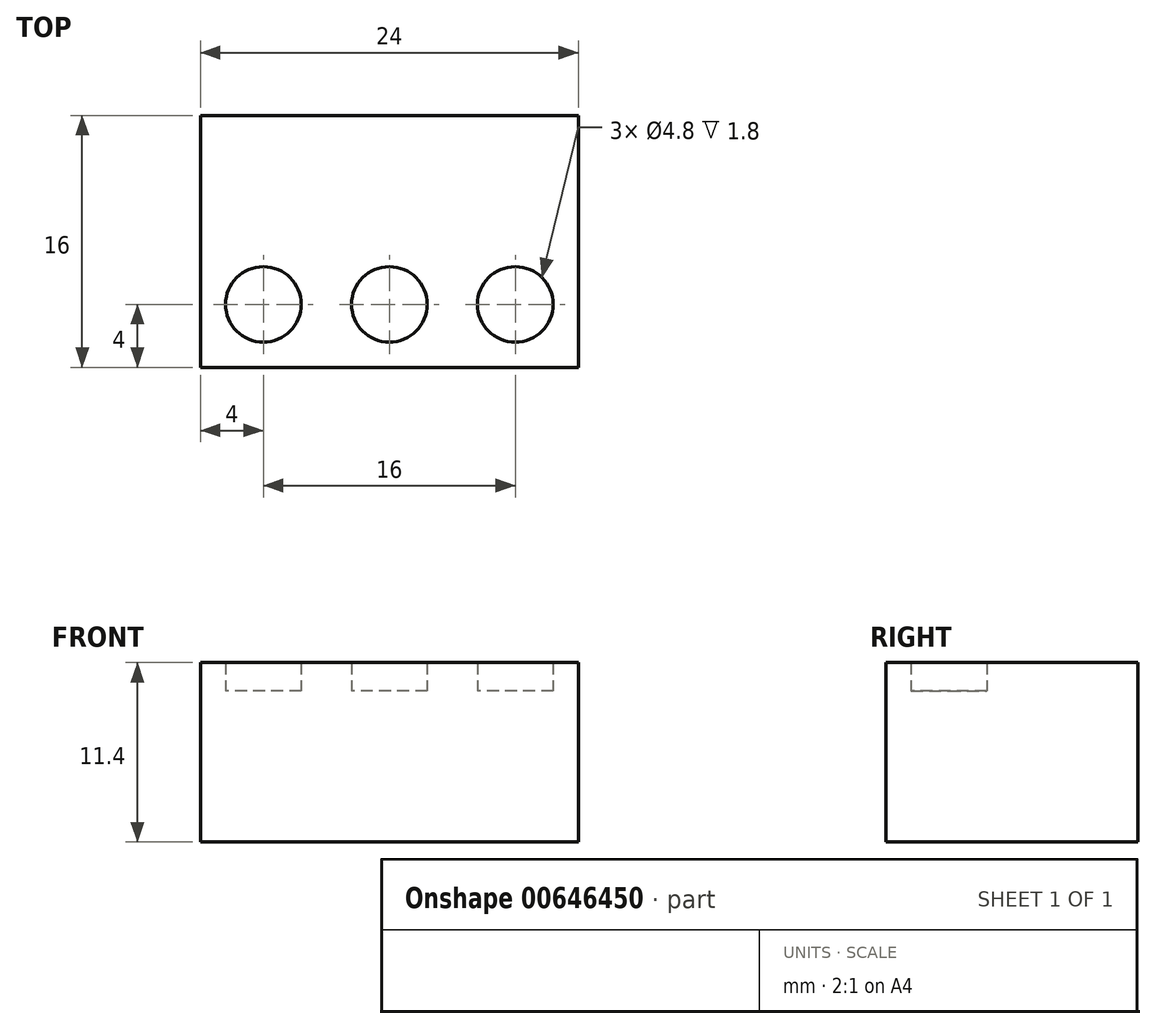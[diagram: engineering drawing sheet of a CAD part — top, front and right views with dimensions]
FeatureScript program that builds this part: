
annotation { "Feature Type Name" : "Feature", "Feature Type Description" : "" }
export const myFeature = defineFeature(function(context is Context, id is Id, definition is map)
    precondition{}
    {
        {
            var Q0;
            Q0=qCreatedBy(makeId("Top.planeOp"),FACE);
            var sketch = newSketch(context, id + "F0", { "sketchPlane" : qUnion([Q0])});
            skLineSegment(sketch, "E0.bottom", {"start": v(0, 0) * mm, "end": v(-24, 0) * mm});
            skLineSegment(sketch, "E0.top", {"start": v(0, 16) * mm, "end": v(-24, 16) * mm});
            skLineSegment(sketch, "E0.left", {"start": v(0, 0) * mm, "end": v(0, 16) * mm});
            skLineSegment(sketch, "E0.right", {"start": v(-24, 0) * mm, "end": v(-24, 16) * mm});
            skSolve(sketch);
        }
        {
            var Q0;
            Q0=makeQuery(id+"F0.imprint","IMPRINT",FACE,{"disambiguationData":[TD([[makeQuery(id+"F0.imprint","IMPRINT",EDGE,{"derivedFrom":sQuery(id+"F0.wireOp",EDGE,"E0.bottom")}),-1.0]])]});
            var Q1;
            Q1 = qSketchRegion(id + "F2", true);
            extrude(context, id + "F1", {"entities" : qUnion([Q0, Q1]), "depth" : 9.6 * mm, "offsetDistance" : 25.4 * mm});
        }
        {
            var Q0;
            Q0=makeQuery(id+"F1.opExtrude","CAP_FACE",FACE,{"disambiguationData":[OSD([sQuery(id+"F0.wireOp",EDGE,"E0.bottom"),sQuery(id+"F0.wireOp",EDGE,"E0.top"),sQuery(id+"F0.wireOp",EDGE,"E0.left"),sQuery(id+"F0.wireOp",EDGE,"E0.right")])],"isStart":false});
            var sketch = newSketch(context, id + "F2", { "sketchPlane" : qUnion([Q0])});
            skLineSegment(sketch, "E1", {"start": v(-24, 8) * mm, "end": v(0, 8) * mm, "construction": true});
            skLineSegment(sketch, "E2", {"start": v(-16, 16) * mm, "end": v(-16, 0) * mm, "construction": true});
            skLineSegment(sketch, "E3", {"start": v(-8, 16) * mm, "end": v(-8, 0) * mm, "construction": true});
            skLineSegment(sketch, "E4", {"start": v(-24, 16) * mm, "end": v(-16, 8) * mm, "construction": true});
            skLineSegment(sketch, "E5", {"start": v(-16, 8) * mm, "end": v(-8, 16) * mm, "construction": true});
            skLineSegment(sketch, "E6", {"start": v(-8, 16) * mm, "end": v(0, 8) * mm, "construction": true});
            skCircle(sketch, "E7", {"center": v(-20, 12) * mm, "radius": 2.4 * mm});
            skCircle(sketch, "E8", {"center": v(-12, 12) * mm, "radius": 2.4 * mm});
            skCircle(sketch, "E9", {"center": v(-4, 12) * mm, "radius": 2.4 * mm});
            skCircle(sketch, "E10.MirrorC", {"center": v(-20, 4) * mm, "radius": 2.4 * mm});
            skCircle(sketch, "E11.MirrorC", {"center": v(-12, 4) * mm, "radius": 2.4 * mm});
            skCircle(sketch, "E12.MirrorC", {"center": v(-4, 4) * mm, "radius": 2.4 * mm});
            skSolve(sketch);
        }
        {
            var Q0;
            Q0=makeQuery(id+"F2.imprint","IMPRINT",FACE,{"disambiguationData":[TD([[makeQuery(id+"F2.imprint","IMPRINT",EDGE,{"derivedFrom":sQuery(id+"F2.wireOp",EDGE,"E7")}),1.0]])]});
            var Q1;
            Q1=makeQuery(id+"F2.imprint","IMPRINT",FACE,{"disambiguationData":[TD([[makeQuery(id+"F2.imprint","IMPRINT",EDGE,{"derivedFrom":sQuery(id+"F2.wireOp",EDGE,"E8")}),1.0]])]});
            var Q2;
            Q2=makeQuery(id+"F2.imprint","IMPRINT",FACE,{"disambiguationData":[TD([[makeQuery(id+"F2.imprint","IMPRINT",EDGE,{"derivedFrom":sQuery(id+"F2.wireOp",EDGE,"E9")}),1.0]])]});
            var Q3;
            Q3=makeQuery(id+"F2.imprint","IMPRINT",FACE,{"disambiguationData":[TD([[makeQuery(id+"F2.imprint","IMPRINT",EDGE,{"derivedFrom":sQuery(id+"F2.wireOp",EDGE,"E10.MirrorC")}),-1.0]])]});
            var Q4;
            Q4=makeQuery(id+"F2.imprint","IMPRINT",FACE,{"disambiguationData":[TD([[makeQuery(id+"F2.imprint","IMPRINT",EDGE,{"derivedFrom":sQuery(id+"F2.wireOp",EDGE,"E11.MirrorC")}),-1.0]])]});
            var Q5;
            Q5=makeQuery(id+"F2.imprint","IMPRINT",FACE,{"disambiguationData":[TD([[makeQuery(id+"F2.imprint","IMPRINT",EDGE,{"derivedFrom":sQuery(id+"F2.wireOp",EDGE,"E12.MirrorC")}),-1.0]])]});
            extrude(context, id + "F3", {"entities" : qUnion([Q0, Q1, Q2, Q3, Q4, Q5]), "operationType" : NewBodyOperationType.ADD, "depth" : 1.8 * mm, "offsetDistance" : 25.4 * mm});
        }
    });
